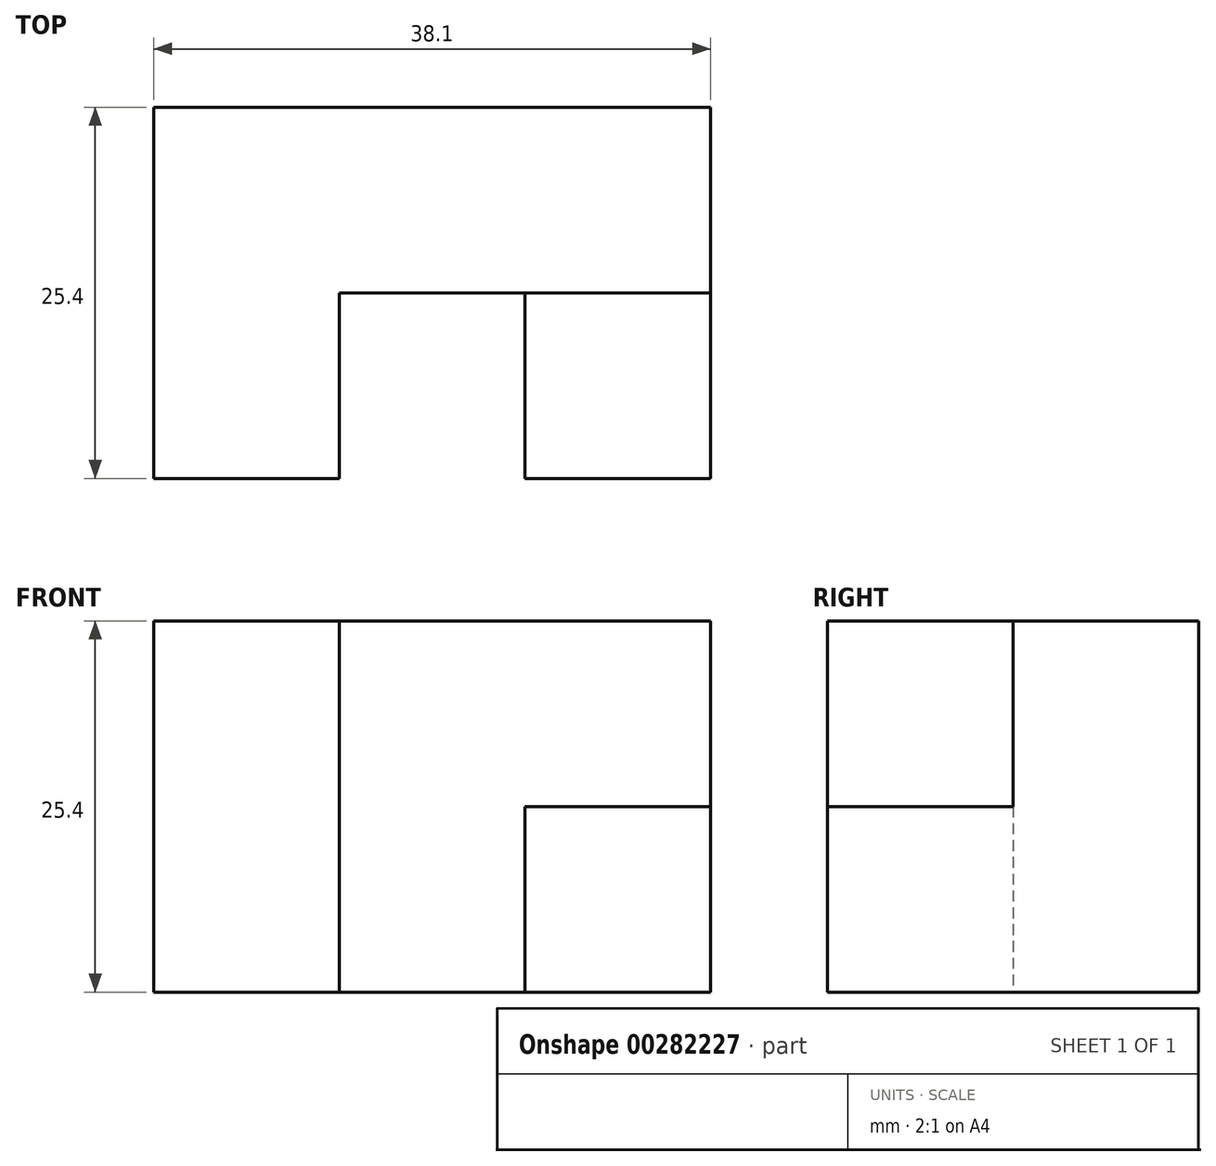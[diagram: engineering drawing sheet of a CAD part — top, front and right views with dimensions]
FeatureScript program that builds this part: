
annotation { "Feature Type Name" : "Feature", "Feature Type Description" : "" }
export const myFeature = defineFeature(function(context is Context, id is Id, definition is map)
    precondition{}
    {
        {
            var Q0;
            Q0=qCreatedBy(makeId("Front.planeOp"),FACE);
            var sketch = newSketch(context, id + "F0", { "sketchPlane" : qUnion([Q0])});
            skLineSegment(sketch, "E0.bottom", {"start": v(0, 0) * mm, "end": v(38.1, 0) * mm});
            skLineSegment(sketch, "E0.top", {"start": v(0, 25.4) * mm, "end": v(38.1, 25.4) * mm});
            skLineSegment(sketch, "E0.left", {"start": v(0, 0) * mm, "end": v(0, 25.4) * mm});
            skLineSegment(sketch, "E0.right", {"start": v(38.1, 0) * mm, "end": v(38.1, 25.4) * mm});
            skSolve(sketch);
        }
        {
            var Q0;
            Q0=makeQuery(id+"F0.imprint","IMPRINT",FACE,{"disambiguationData":[TD([[makeQuery(id+"F0.imprint","IMPRINT",EDGE,{"derivedFrom":sQuery(id+"F0.wireOp",EDGE,"E0.bottom")}),1.0]])]});
            extrude(context, id + "F1", {"entities" : qUnion([Q0]), "depth" : 25.4 * mm});
        }
        {
            var Q0;
            Q0=makeQuery(id+"F1.opExtrude","CAP_FACE",FACE,{"disambiguationData":[OSD([sQuery(id+"F0.wireOp",EDGE,"E0.bottom"),sQuery(id+"F0.wireOp",EDGE,"E0.top"),sQuery(id+"F0.wireOp",EDGE,"E0.left"),sQuery(id+"F0.wireOp",EDGE,"E0.right")])],"isStart":false});
            var sketch = newSketch(context, id + "F2", { "sketchPlane" : qUnion([Q0])});
            skLineSegment(sketch, "E1", {"start": v(12.7, 0) * mm, "end": v(12.7, 25.4) * mm});
            skLineSegment(sketch, "E2", {"start": v(12.7, 25.4) * mm, "end": v(38.1, 25.4) * mm});
            skLineSegment(sketch, "E3", {"start": v(38.1, 25.4) * mm, "end": v(38.1, 12.7) * mm});
            skLineSegment(sketch, "E4", {"start": v(38.1, 12.7) * mm, "end": v(25.4, 12.7) * mm});
            skLineSegment(sketch, "E5", {"start": v(25.4, 12.7) * mm, "end": v(25.4, 0) * mm});
            skSolve(sketch);
        }
        {
            var Q0;
            {var subQ0=sQuery(id+"F2.wireOp",EDGE,"E1");Q0=makeQuery(id+"F2.imprint","IMPRINT",FACE,{"disambiguationData":[TD([[makeQuery(id+"F2.imprint","IMPRINT",EDGE,{"derivedFrom":subQ0}),-1.0]])]});}
            extrude(context, id + "F3", {"entities" : qUnion([Q0]), "operationType" : NewBodyOperationType.REMOVE, "oppositeDirection" : true, "depth" : 12.7 * mm});
        }
    });
